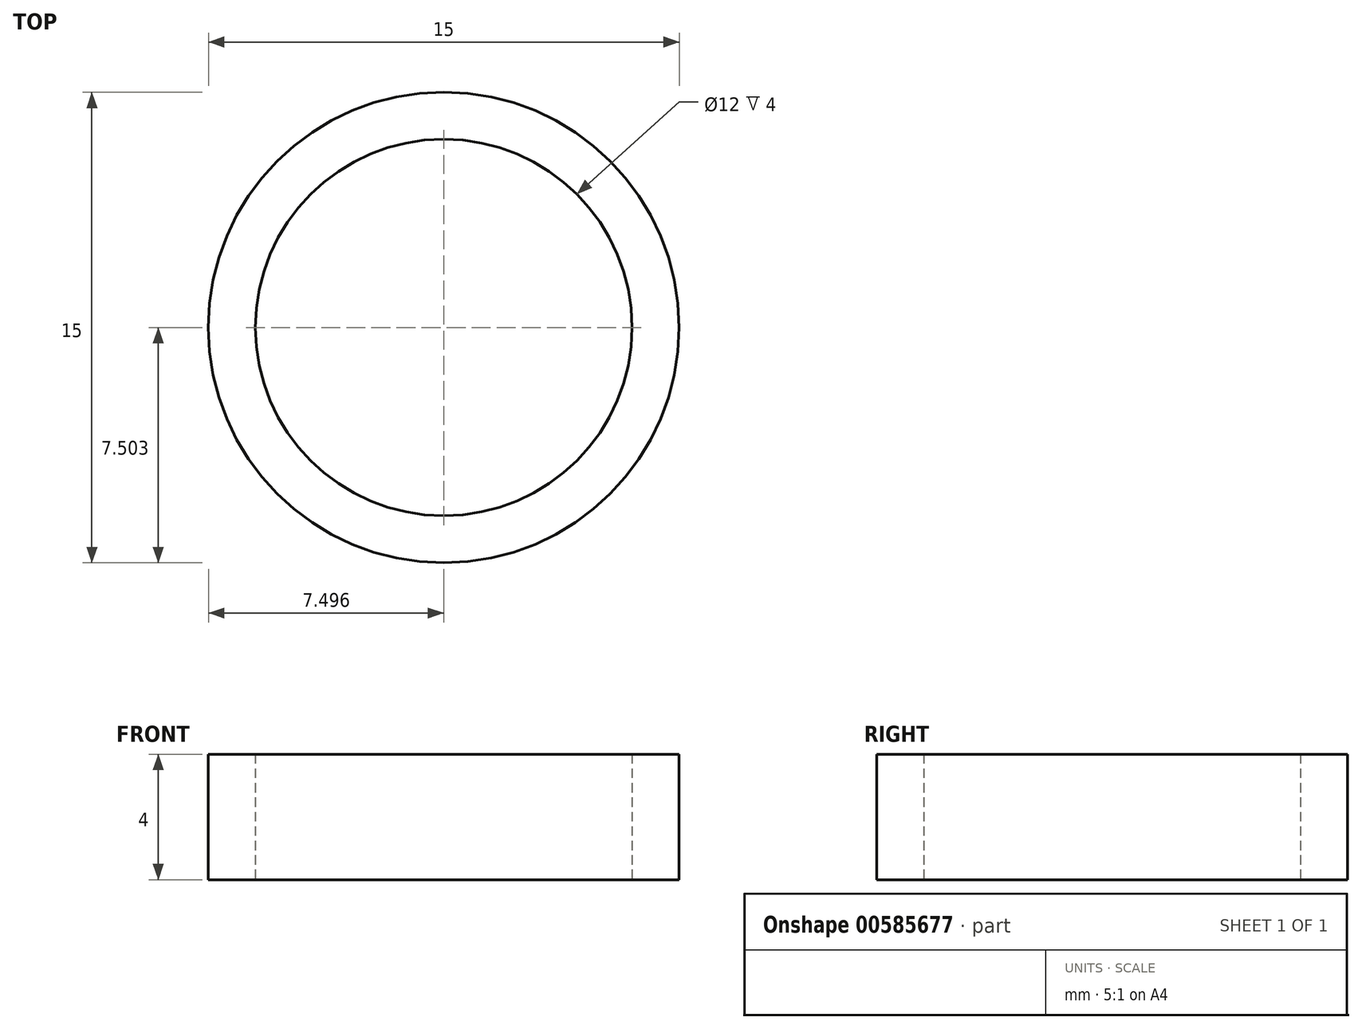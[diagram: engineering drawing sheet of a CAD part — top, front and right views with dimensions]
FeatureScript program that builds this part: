
annotation { "Feature Type Name" : "Feature", "Feature Type Description" : "" }
export const myFeature = defineFeature(function(context is Context, id is Id, definition is map)
    precondition{}
    {
        {
            var Q0;
            Q0=qCreatedBy(makeId("Top.planeOp"),FACE);
            var sketch = newSketch(context, id + "F0", { "sketchPlane" : qUnion([Q0])});
            skCircle(sketch, "E0", {"center": v(3.03, 2.15) * mm, "radius": 7.5 * mm});
            skCircle(sketch, "E1", {"center": v(3.03, 2.15) * mm, "radius": 6 * mm});
            skSolve(sketch);
        }
        {
            var Q0;
            Q0 = qSketchRegion(id + "F0", true);
            extrude(context, id + "F1", {"entities" : qUnion([Q0]), "depth" : 4 * mm, "offsetDistance" : 25 * mm});
        }
    });
